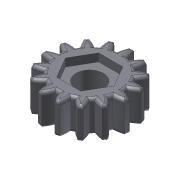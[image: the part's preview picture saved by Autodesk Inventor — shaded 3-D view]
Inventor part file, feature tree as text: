
AUTODESK INVENTOR PART (.ipt)
format: ipt  version: 2015 SP2 (Build 190223200, 223)  size: 588,800 bytes
history: native  units: mm (DEFAULTED — no unit token found)
features: sketch x4, extrude x3, plane x3, other x3, fillet x3
ambient origin geometry x8: Origin, YZ Plane, XZ Plane, XY Plane, X Axis, Y Axis, Z Axis, Center Point
bodies: Body1 (feature_tree), Body2 (feature_tree)
feature tree (16):
  extrude  "Extrusion1"  Depth=10.0mm TaperAngle=0.0deg
  plane  "Work Plane2"
  plane  "Work Plane8"
  plane  "Work Plane9"
  other  "Engranaje recto"
  extrude  "Extrusión3"  Depth=10.0mm TaperAngle=0.0deg
  extrude  "Extrusión4"  Depth=2.094395mm TaperAngle=0.0deg
  fillet  "Empalme1"  [1 undecoded]
  fillet  "Empalme2"  [1 undecoded]
  fillet  "Empalme3"  Radius=19.0mm
  sketch  "Sketch1"  dims[d0=26.8mm d1=10.0mm d2=0.0mm]
  sketch  "Sketch2"  dims[d3=24.782609mm d4=10.0mm d5=0.0mm]
  other  "Srf1"
  sketch  "Boceto4"  dims[d16=19.0mm d17=0.0mm d34=2.094395mm d39=0.0mm d41=0.0mm d43=19.0mm]
  sketch  "Boceto5"  dims[d46=19.0mm d47=0.0mm d48=0.0mm d52=13.4mm d53=2.5mm d54=0.0mm d55=8.7mm d56=2.5mm d57=0.0mm d58=1.0mm d59=1.0mm d60=1.0mm]
  other  "Diámetro de separación"
note: 2 required parameter values undecoded (feature->parameter linkage not recoverable at this tier; creation-order binding heuristic only, values carry confidence <= 0.55)
